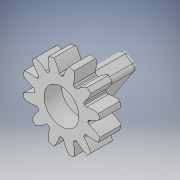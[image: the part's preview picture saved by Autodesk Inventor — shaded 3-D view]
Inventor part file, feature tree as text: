
AUTODESK INVENTOR PART (.ipt)
format: ipt  version: 2019 (Build 230136000, 136)  size: 397,824 bytes
history: native  units: in
note: dims shown in document units (in); Inventor stores cm internally (conversion verified against a paired STEP export)
features: extrude x4, sketch x4, pattern_circular x2, fillet x2, projected_geometry x1
ambient origin geometry x8: Origin, YZ Plane, XZ Plane, XY Plane, X Axis, Y Axis, Z Axis, Center Point
bodies: Solid1 (feature_tree)
feature tree (13):
  extrude  "Extrusion1"  Depth=0.1969in
  extrude  "Extrusion2"  Depth=1.0in
  pattern_circular  "Circular Pattern1"  [2 undecoded]
  extrude  "Extrusion3"  Depth=0.0394in
  extrude  "Extrusion4"  Depth=0.0394in TaperAngle=0.0deg
  fillet  "Fillet1"  Radius=7.874in
  fillet  "Fillet3"  Radius=0.0394in
  sketch  "Sketch1"  dims[d0=1.0in d2=0.1969in]
  projected_geometry  "Projected Loop1"
  sketch  "Sketch3"  dims[d3=1.0in d4=0.0in d7=0.0591in]
  sketch  "Sketch4"  dims[d9=0.3937in]
  sketch  "Sketch5"  dims[d10=0.4724in d11=0.0197in d12=0.0591in d13=0.0787in d14=0.0in d15=7.874in d16=2.4737in d19=0.0394in d20=0.0in d21=0.4724in d22=0.1575in d23=0.315in d24=0.0in d25=0.0394in d27=0.0394in]
  pattern_circular  "CirPattern1"
note: 2 required parameter values undecoded (feature->parameter linkage not recoverable at this tier; creation-order binding heuristic only, values carry confidence <= 0.55)
